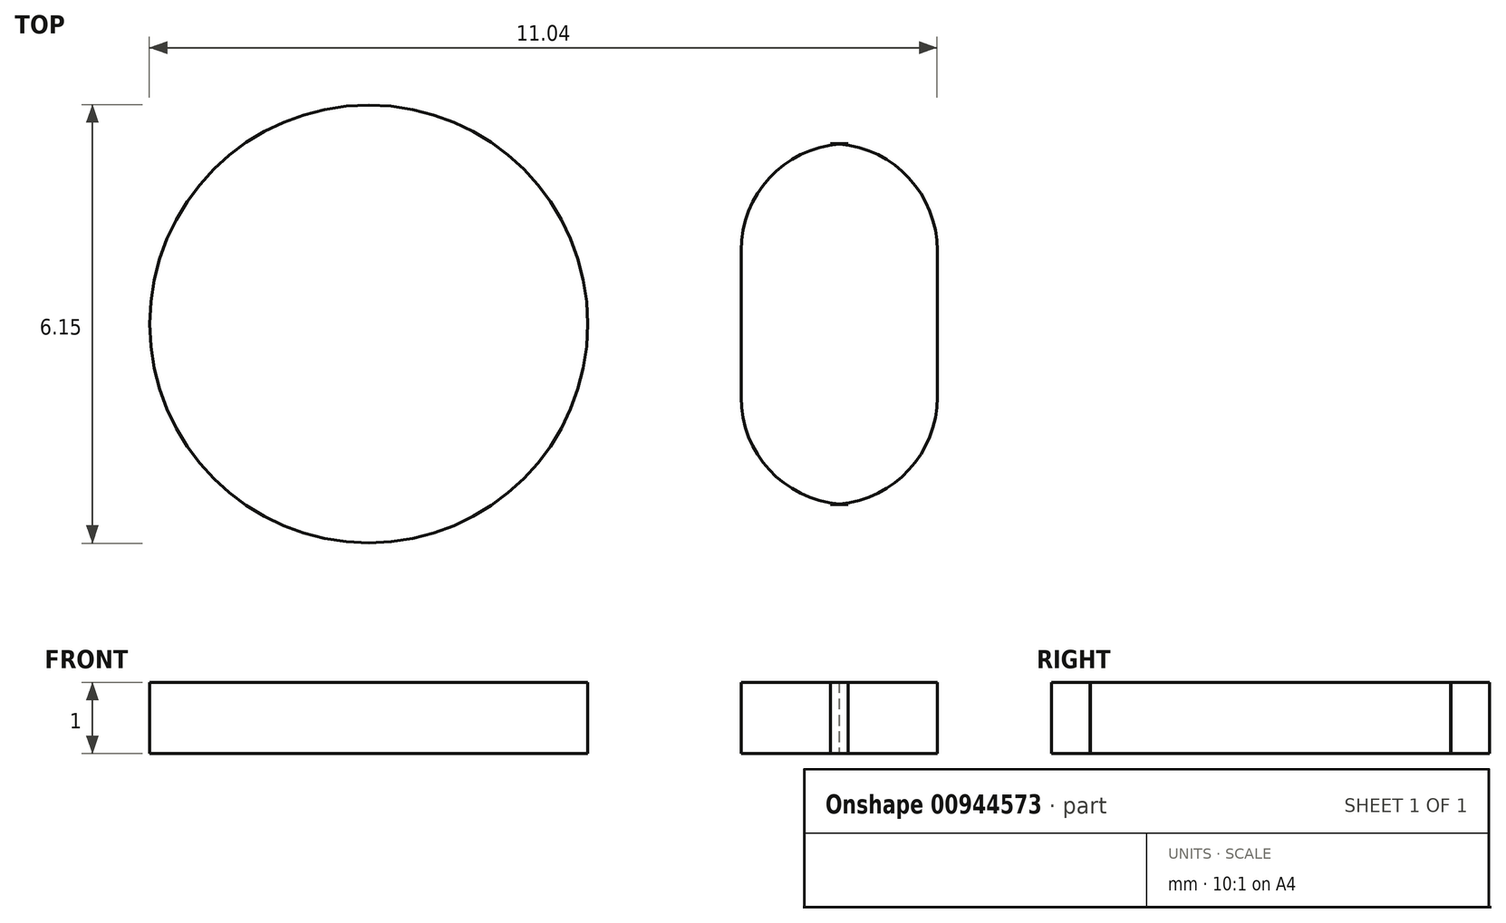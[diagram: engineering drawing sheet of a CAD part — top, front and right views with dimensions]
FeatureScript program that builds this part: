
annotation { "Feature Type Name" : "Feature", "Feature Type Description" : "" }
export const myFeature = defineFeature(function(context is Context, id is Id, definition is map)
    precondition{}
    {
        {
            var Q0;
            Q0=qCreatedBy(makeId("Top.planeOp"),FACE);
            var sketch = newSketch(context, id + "F0", { "sketchPlane" : qUnion([Q0])});
            skLineSegment(sketch, "E0.bottom", {"start": v(20.29, 61.91) * mm, "end": v(-20.28, 61.91) * mm});
            skLineSegment(sketch, "E0.top", {"start": v(20.28, -61.91) * mm, "end": v(-20.29, -61.92) * mm});
            skLineSegment(sketch, "E0.left", {"start": v(29.29, 52.91) * mm, "end": v(29.29, -52.91) * mm});
            skLineSegment(sketch, "E0.right", {"start": v(-29.29, 52.91) * mm, "end": v(-29.28, -52.91) * mm});
            skPoint(sketch, "E0.middle", {"position": v(0, 0) * mm});
            skPoint(sketch, "E1.visualSharp", {"position": v(-29.29, 61.91) * mm});
            skArc(sketch, "E1.filletArc", {"start": v(-20.28, 61.91) * mm, "mid": v(-26.65, 59.28) * mm, "end": v(-29.29, 52.91) * mm});
            skPoint(sketch, "E2.visualSharp", {"position": v(-29.29, -61.91) * mm});
            skArc(sketch, "E2.filletArc", {"start": v(-29.29, -52.91) * mm, "mid": v(-26.65, -59.28) * mm, "end": v(-20.29, -61.91) * mm});
            skPoint(sketch, "E3.visualSharp", {"position": v(29.29, -61.91) * mm});
            skArc(sketch, "E3.filletArc", {"start": v(20.28, -61.91) * mm, "mid": v(26.65, -59.28) * mm, "end": v(29.29, -52.91) * mm});
            skPoint(sketch, "E4.visualSharp", {"position": v(29.29, 61.91) * mm});
            skArc(sketch, "E4.filletArc", {"start": v(29.29, 52.91) * mm, "mid": v(26.65, 59.28) * mm, "end": v(20.29, 61.91) * mm});
            skSolve(sketch);
        }
        {
            var Q0;
            Q0=makeQuery(id+"F0.imprint","IMPRINT",FACE,{"disambiguationData":[TD([[makeQuery(id+"F0.imprint","IMPRINT",EDGE,{"derivedFrom":sQuery(id+"F0.wireOp",EDGE,"E0.bottom")}),1.0]])]});
            extrude(context, id + "F1", {"entities" : qUnion([Q0]), "depth" : 1 * mm, "offsetDistance" : 25 * mm});
        }
        {
            var Q0;
            Q0=qCreatedBy(makeId("Top.planeOp"),FACE);
            var sketch = newSketch(context, id + "F2", { "sketchPlane" : qUnion([Q0])});
            skCircle(sketch, "E5", {"center": v(-20, 54.56) * mm, "radius": 3.07 * mm});
            skLineSegment(sketch, "E6.bottom", {"start": v(-13.29, 52.03) * mm, "end": v(-13.54, 52.03) * mm});
            skLineSegment(sketch, "E6.top", {"start": v(-13.29, 57.1) * mm, "end": v(-13.54, 57.1) * mm});
            skLineSegment(sketch, "E6.left", {"start": v(-12.04, 53.53) * mm, "end": v(-12.04, 55.6) * mm});
            skLineSegment(sketch, "E6.right", {"start": v(-14.79, 53.53) * mm, "end": v(-14.79, 55.6) * mm});
            skPoint(sketch, "E6.middle", {"position": v(-13.41, 54.56) * mm});
            skPoint(sketch, "E7.visualSharp", {"position": v(-14.79, 57.1) * mm});
            skArc(sketch, "E7.filletArc", {"start": v(-13.29, 57.1) * mm, "mid": v(-14.35, 56.66) * mm, "end": v(-14.79, 55.6) * mm});
            skPoint(sketch, "E8.visualSharp", {"position": v(-12.04, 57.1) * mm});
            skArc(sketch, "E8.filletArc", {"start": v(-12.04, 55.6) * mm, "mid": v(-12.47, 56.66) * mm, "end": v(-13.54, 57.1) * mm});
            skPoint(sketch, "E9.visualSharp", {"position": v(-12.04, 52.03) * mm});
            skArc(sketch, "E9.filletArc", {"start": v(-13.54, 52.03) * mm, "mid": v(-12.47, 52.47) * mm, "end": v(-12.04, 53.53) * mm});
            skPoint(sketch, "E10.visualSharp", {"position": v(-14.79, 52.03) * mm});
            skArc(sketch, "E10.filletArc", {"start": v(-14.79, 53.53) * mm, "mid": v(-14.35, 52.47) * mm, "end": v(-13.29, 52.03) * mm});
            skSolve(sketch);
        }
        {
            var Q0;
            Q0 = qSketchRegion(id + "F2", true);
            extrude(context, id + "F3", {"entities" : qUnion([Q0]), "operationType" : NewBodyOperationType.INTERSECT, "depth" : 25 * mm, "offsetDistance" : 25 * mm});
        }
    });
